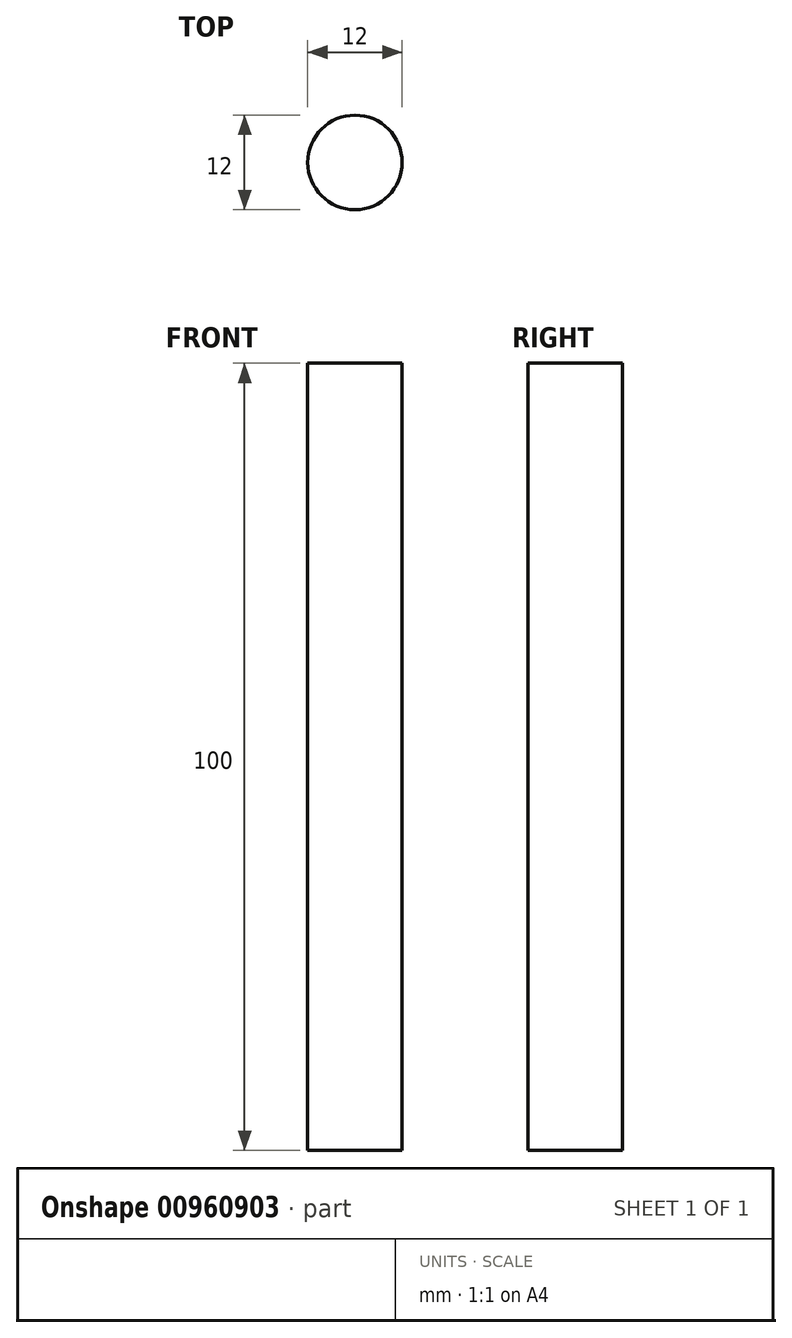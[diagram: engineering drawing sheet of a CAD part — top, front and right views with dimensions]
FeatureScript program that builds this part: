
annotation { "Feature Type Name" : "Feature", "Feature Type Description" : "" }
export const myFeature = defineFeature(function(context is Context, id is Id, definition is map)
    precondition{}
    {
        {
            var Q0;
            Q0=qCreatedBy(makeId("Top.planeOp"), FACE);
            var sketch = newSketch(context, id + "F0", { "sketchPlane" : qUnion([Q0])});
            skCircle(sketch, "E0", {"center": v(0, 0) * mm, "radius": 6 * mm});
            skSolve(sketch);
        }
        {
            var Q0;
            Q0 = qSketchRegion(id + "F0", true);
            extrude(context, id + "F1", {"entities" : qUnion([Q0]), "domain" : OperationDomain.MODEL, "flatOperationType" : FlatOperationType.REMOVE, "depth" : 100 * mm, "offsetDistance" : 25 * mm});
        }
    });
